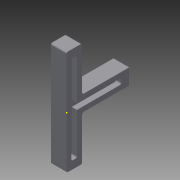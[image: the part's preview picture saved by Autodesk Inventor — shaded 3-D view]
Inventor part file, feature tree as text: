
AUTODESK INVENTOR PART (.ipt)
format: ipt  version: 2015 (Build 190159000, 159)  size: 138,752 bytes
history: native  units: mm
features: fillet x12, sketch x3, extrude x2, other x1
ambient origin geometry x8: Origin, YZ Plane, XZ Plane, XY Plane, X Axis, Y Axis, Z Axis, Center Point
bodies: Body1 (feature_tree)
feature tree (18):
  other  "ソリッド1"
  extrude  "押し出し1"  Depth=30.0mm
  sketch  "スケッチ2"
  sketch  "スケッチ3"
  extrude  "押し出し2"  Depth=120.0mm
  fillet  "フィレット1"  Radius=30.0mm
  fillet  "フィレット2"  Radius=200.0mm
  fillet  "フィレット3"  Radius=30.0mm
  fillet  "フィレット4"  Radius=11.0mm
  fillet  "フィレット5"  Radius=11.0mm
  fillet  "フィレット6"  Radius=170.0mm
  fillet  "フィレット7"  Radius=9.0mm
  fillet  "フィレット8"  Radius=11.0mm
  fillet  "フィレット9"  Radius=85.0mm
  fillet  "フィレット10"  Radius=10.0mm
  fillet  "フィレット11"  Radius=3.0mm
  fillet  "フィレット12"  Radius=3.0mm
  sketch  "スケッチ1"
